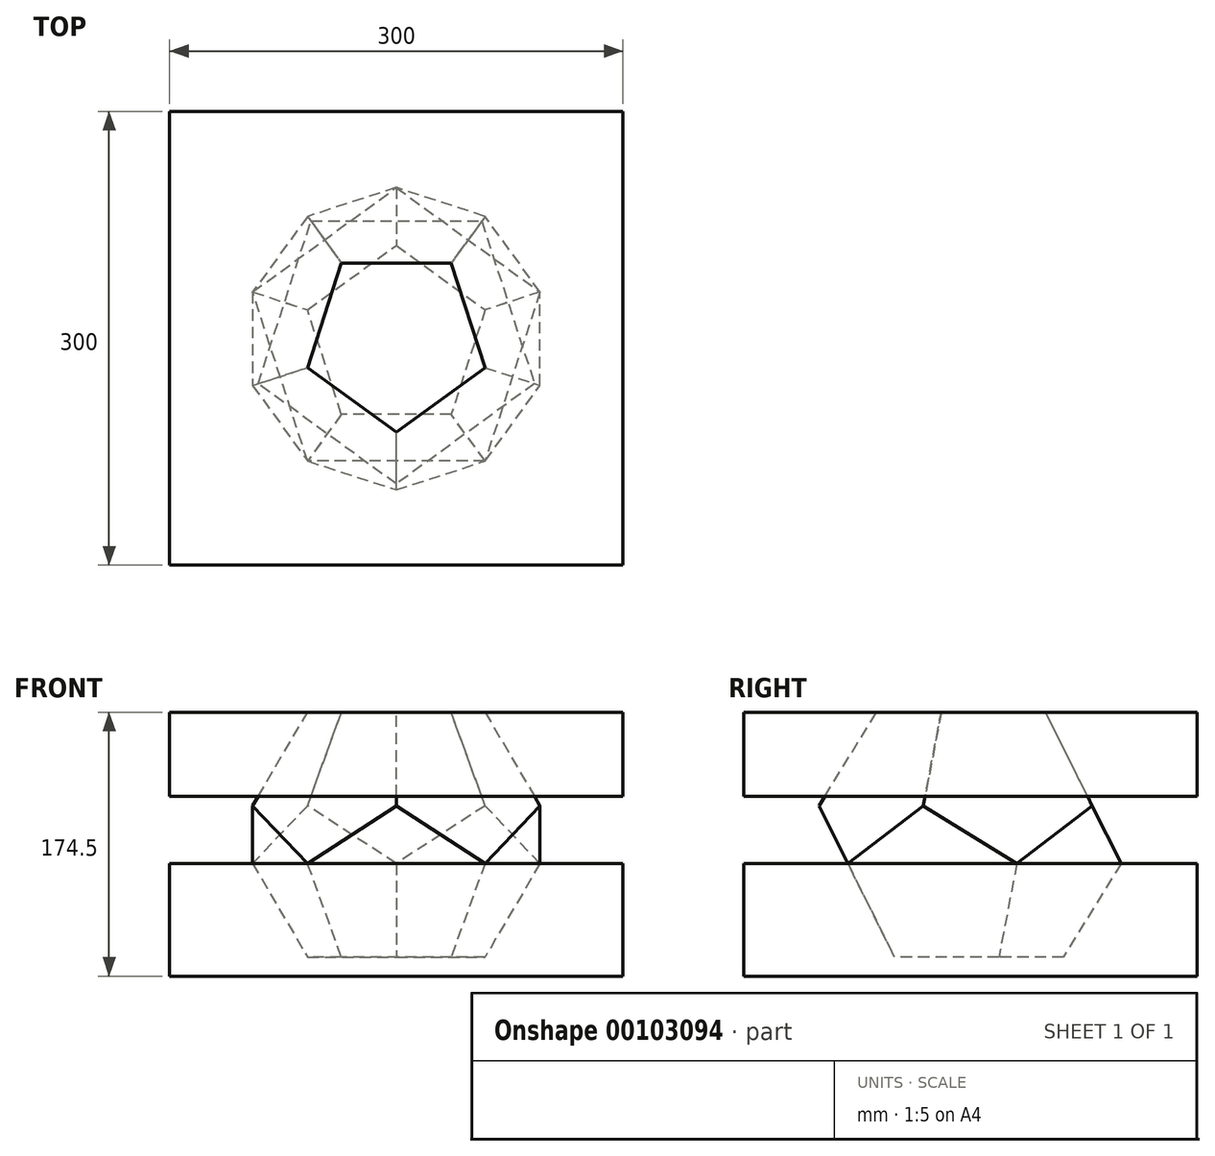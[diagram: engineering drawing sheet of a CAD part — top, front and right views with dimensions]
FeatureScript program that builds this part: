
annotation { "Feature Type Name" : "Feature", "Feature Type Description" : "" }
export const myFeature = defineFeature(function(context is Context, id is Id, definition is map)
    precondition{}
    {
        {
            var Q0;
            Q0=qCreatedBy(makeId("Top.planeOp"),FACE);
            var sketch = newSketch(context, id + "F0", { "sketchPlane" : qUnion([Q0])});
            skCircle(sketch, "E0.cCircle", {"center": v(0, 0) * mm, "radius": 50 * mm, "construction": true});
            skLineSegment(sketch, "E0.0", {"start": v(0, 61.8) * mm, "end": v(58.78, 19.1) * mm});
            skLineSegment(sketch, "E0.1", {"start": v(58.78, 19.1) * mm, "end": v(36.33, -50) * mm});
            skLineSegment(sketch, "E0.2", {"start": v(36.33, -50) * mm, "end": v(-36.33, -50) * mm});
            skLineSegment(sketch, "E0.3", {"start": v(-36.33, -50) * mm, "end": v(-58.78, 19.1) * mm});
            skLineSegment(sketch, "E0.4", {"start": v(-58.78, 19.1) * mm, "end": v(0, 61.8) * mm});
            skPoint(sketch, "E0.0.midPoint", {"position": v(29.39, 40.45) * mm});
            skSolve(sketch);
        }
        {
            var Q0;
            Q0=qCreatedBy(makeId("Right.planeOp"),FACE);
            var sketch = newSketch(context, id + "F1", { "sketchPlane" : qUnion([Q0])});
            skLineSegment(sketch, "E1", {"start": v(-50, 0) * mm, "end": v(-75.48, 50.96) * mm, "construction": true});
            skLineSegment(sketch, "E2", {"start": v(-50, 0) * mm, "end": v(0, 0) * mm, "construction": true});
            skLineSegment(sketch, "E3", {"start": v(0, 0) * mm, "end": v(0, 50.96) * mm, "construction": true});
            skSolve(sketch);
        }
        {
            var Q0;
            Q0=sQuery(id+"F0.wireOp",VERTEX,"E0.1.end");
            var Q1;
            Q1=sQuery(id+"F1.wireOp",VERTEX,"E1.start");
            var Q2;
            Q2=sQuery(id+"F1.wireOp",VERTEX,"E1.end");
            cPlane(context, id + "F2", {"entities" : qUnion([Q0, Q1, Q2]), "cplaneType" : CPlaneType.THREE_POINT, "offset" : 150 * mm, "width" : 150 * mm, "height" : 150 * mm});
        }
        {
            var Q0;
            Q0=qCreatedBy(id+"F2.planeOp",FACE);
            var sketch = newSketch(context, id + "F3", { "sketchPlane" : qUnion([Q0])});
            skCircle(sketch, "E4.cCircle", {"center": v(0, 72.36) * mm, "radius": 50 * mm, "construction": true});
            skLineSegment(sketch, "E4.0", {"start": v(36.33, 22.36) * mm, "end": v(-36.33, 22.36) * mm});
            skLineSegment(sketch, "E4.1", {"start": v(-36.33, 22.36) * mm, "end": v(-58.78, 91.46) * mm});
            skLineSegment(sketch, "E4.2", {"start": v(-58.78, 91.46) * mm, "end": v(0, 134.16) * mm});
            skLineSegment(sketch, "E4.3", {"start": v(0, 134.16) * mm, "end": v(58.78, 91.46) * mm});
            skLineSegment(sketch, "E4.4", {"start": v(58.78, 91.46) * mm, "end": v(36.33, 22.36) * mm});
            skPoint(sketch, "E4.0.midPoint", {"position": v(0, 22.36) * mm});
            skSolve(sketch);
        }
        {
            var Q0;
            Q0=qCreatedBy(makeId("Right.planeOp"),FACE);
            var sketch = newSketch(context, id + "F4", { "sketchPlane" : qUnion([Q0])});
            skLineSegment(sketch, "E5.0", {"start": v(-100, 100) * mm, "end": v(-80.9, 61.8) * mm, "construction": true});
            skLineSegment(sketch, "E6", {"start": v(-90.45, 80.9) * mm, "end": v(61.8, 80.9) * mm, "construction": true});
            skSolve(sketch);
        }
        {
            var Q0;
            Q0=makeQuery(id+"F0.imprint","IMPRINT",FACE,{"disambiguationData":[TD([[makeQuery(id+"F0.imprint","IMPRINT",EDGE,{"derivedFrom":sQuery(id+"F0.wireOp",EDGE,"E0.0")}),-1.0]])]});
            var Q1;
            Q1=qCreatedBy(id+"F2.planeOp",FACE);
            extrude(context, id + "F5", {"entities" : qUnion([Q0]), "endBoundEntity" : qUnion([Q1]), "depth" : 40 * mm});
        }
        {
            var Q0;
            Q0=makeQuery(id+"F3.imprint","IMPRINT",FACE,{"disambiguationData":[TD([[makeQuery(id+"F3.imprint","IMPRINT",EDGE,{"derivedFrom":sQuery(id+"F3.wireOp",EDGE,"E4.0")}),-1.0]])]});
            extrude(context, id + "F6", {"entities" : qUnion([Q0]), "oppositeDirection" : true, "depth" : 120 * mm});
        }
        {
            var Q0;
            Q0=makeQuery(id+"F6.opExtrude","SWEPT_BODY",BODY,{"disambiguationData":[OSD([sQuery(id+"F3.wireOp",EDGE,"E4.0"),sQuery(id+"F3.wireOp",EDGE,"E4.1"),sQuery(id+"F3.wireOp",EDGE,"E4.2"),sQuery(id+"F3.wireOp",EDGE,"E4.3"),sQuery(id+"F3.wireOp",EDGE,"E4.4")])]});
            var Q1;
            Q1=sQuery(id+"F1.wireOp",EDGE,"E3");
            circularPattern(context, id + "F7", {"entities" : qUnion([Q0]), "axis" : qUnion([Q1]), "angle" : 72 * degree, "instanceCount" : 5});
        }
        {
            var Q0;
            Q0=makeQuery(id+"F5.opExtrude","SWEPT_BODY",BODY,{"disambiguationData":[OSD([sQuery(id+"F0.wireOp",EDGE,"E0.0"),sQuery(id+"F0.wireOp",EDGE,"E0.1"),sQuery(id+"F0.wireOp",EDGE,"E0.2"),sQuery(id+"F0.wireOp",EDGE,"E0.3"),sQuery(id+"F0.wireOp",EDGE,"E0.4")])]});
            var Q1;
            Q1=makeQuery(id+"F6.opExtrude","SWEPT_BODY",BODY,{"disambiguationData":[OSD([sQuery(id+"F3.wireOp",EDGE,"E4.0"),sQuery(id+"F3.wireOp",EDGE,"E4.1"),sQuery(id+"F3.wireOp",EDGE,"E4.2"),sQuery(id+"F3.wireOp",EDGE,"E4.3"),sQuery(id+"F3.wireOp",EDGE,"E4.4")])]});
            var Q2;
            Q2=makeQuery(id+"F7.opPattern","COPY",BODY,{"derivedFrom":makeQuery(id+"F6.opExtrude","SWEPT_BODY",BODY,{"disambiguationData":[OSD([sQuery(id+"F3.wireOp",EDGE,"E4.0"),sQuery(id+"F3.wireOp",EDGE,"E4.1"),sQuery(id+"F3.wireOp",EDGE,"E4.2"),sQuery(id+"F3.wireOp",EDGE,"E4.3"),sQuery(id+"F3.wireOp",EDGE,"E4.4")])]}),"instanceName":"1"});
            var Q3;
            Q3=makeQuery(id+"F7.opPattern","COPY",BODY,{"derivedFrom":makeQuery(id+"F6.opExtrude","SWEPT_BODY",BODY,{"disambiguationData":[OSD([sQuery(id+"F3.wireOp",EDGE,"E4.0"),sQuery(id+"F3.wireOp",EDGE,"E4.1"),sQuery(id+"F3.wireOp",EDGE,"E4.2"),sQuery(id+"F3.wireOp",EDGE,"E4.3"),sQuery(id+"F3.wireOp",EDGE,"E4.4")])]}),"instanceName":"2"});
            var Q4;
            Q4=makeQuery(id+"F7.opPattern","COPY",BODY,{"derivedFrom":makeQuery(id+"F6.opExtrude","SWEPT_BODY",BODY,{"disambiguationData":[OSD([sQuery(id+"F3.wireOp",EDGE,"E4.0"),sQuery(id+"F3.wireOp",EDGE,"E4.1"),sQuery(id+"F3.wireOp",EDGE,"E4.2"),sQuery(id+"F3.wireOp",EDGE,"E4.3"),sQuery(id+"F3.wireOp",EDGE,"E4.4")])]}),"instanceName":"3"});
            var Q5;
            Q5=makeQuery(id+"F7.opPattern","COPY",BODY,{"derivedFrom":makeQuery(id+"F6.opExtrude","SWEPT_BODY",BODY,{"disambiguationData":[OSD([sQuery(id+"F3.wireOp",EDGE,"E4.0"),sQuery(id+"F3.wireOp",EDGE,"E4.1"),sQuery(id+"F3.wireOp",EDGE,"E4.2"),sQuery(id+"F3.wireOp",EDGE,"E4.3"),sQuery(id+"F3.wireOp",EDGE,"E4.4")])]}),"instanceName":"4"});
            var Q6;
            Q6=sQuery(id+"F4.wireOp",EDGE,"E6");
            transform(context, id + "F8", {"entities" : qUnion([Q0, Q1, Q2, Q3, Q4, Q5]), "transformType" : TransformType.ROTATION, "transformAxis" : qUnion([Q6]), "angle" : 180 * degree, "oppositeX" : false, "oppositeY" : false, "oppositeZ" : false, "makeCopy" : true});
        }
        {
            var Q0;
            Q0=makeQuery(id+"F8.opPattern","COPY",BODY,{"derivedFrom":makeQuery(id+"F7.opPattern","COPY",BODY,{"derivedFrom":makeQuery(id+"F6.opExtrude","SWEPT_BODY",BODY,{"disambiguationData":[OSD([sQuery(id+"F3.wireOp",EDGE,"E4.0"),sQuery(id+"F3.wireOp",EDGE,"E4.1"),sQuery(id+"F3.wireOp",EDGE,"E4.2"),sQuery(id+"F3.wireOp",EDGE,"E4.3"),sQuery(id+"F3.wireOp",EDGE,"E4.4")])]}),"instanceName":"2"}),"instanceName":"1"});
            var Q1;
            Q1=makeQuery(id+"F8.opPattern","COPY",BODY,{"derivedFrom":makeQuery(id+"F7.opPattern","COPY",BODY,{"derivedFrom":makeQuery(id+"F6.opExtrude","SWEPT_BODY",BODY,{"disambiguationData":[OSD([sQuery(id+"F3.wireOp",EDGE,"E4.0"),sQuery(id+"F3.wireOp",EDGE,"E4.1"),sQuery(id+"F3.wireOp",EDGE,"E4.2"),sQuery(id+"F3.wireOp",EDGE,"E4.3"),sQuery(id+"F3.wireOp",EDGE,"E4.4")])]}),"instanceName":"1"}),"instanceName":"1"});
            var Q2;
            Q2=makeQuery(id+"F8.opPattern","COPY",BODY,{"derivedFrom":makeQuery(id+"F6.opExtrude","SWEPT_BODY",BODY,{"disambiguationData":[OSD([sQuery(id+"F3.wireOp",EDGE,"E4.0"),sQuery(id+"F3.wireOp",EDGE,"E4.1"),sQuery(id+"F3.wireOp",EDGE,"E4.2"),sQuery(id+"F3.wireOp",EDGE,"E4.3"),sQuery(id+"F3.wireOp",EDGE,"E4.4")])]}),"instanceName":"1"});
            var Q3;
            Q3=makeQuery(id+"F8.opPattern","COPY",BODY,{"derivedFrom":makeQuery(id+"F7.opPattern","COPY",BODY,{"derivedFrom":makeQuery(id+"F6.opExtrude","SWEPT_BODY",BODY,{"disambiguationData":[OSD([sQuery(id+"F3.wireOp",EDGE,"E4.0"),sQuery(id+"F3.wireOp",EDGE,"E4.1"),sQuery(id+"F3.wireOp",EDGE,"E4.2"),sQuery(id+"F3.wireOp",EDGE,"E4.3"),sQuery(id+"F3.wireOp",EDGE,"E4.4")])]}),"instanceName":"4"}),"instanceName":"1"});
            var Q4;
            Q4=makeQuery(id+"F8.opPattern","COPY",BODY,{"derivedFrom":makeQuery(id+"F7.opPattern","COPY",BODY,{"derivedFrom":makeQuery(id+"F6.opExtrude","SWEPT_BODY",BODY,{"disambiguationData":[OSD([sQuery(id+"F3.wireOp",EDGE,"E4.0"),sQuery(id+"F3.wireOp",EDGE,"E4.1"),sQuery(id+"F3.wireOp",EDGE,"E4.2"),sQuery(id+"F3.wireOp",EDGE,"E4.3"),sQuery(id+"F3.wireOp",EDGE,"E4.4")])]}),"instanceName":"3"}),"instanceName":"1"});
            var Q5;
            Q5=makeQuery(id+"F8.opPattern","COPY",BODY,{"derivedFrom":makeQuery(id+"F5.opExtrude","SWEPT_BODY",BODY,{"disambiguationData":[OSD([sQuery(id+"F0.wireOp",EDGE,"E0.0"),sQuery(id+"F0.wireOp",EDGE,"E0.1"),sQuery(id+"F0.wireOp",EDGE,"E0.2"),sQuery(id+"F0.wireOp",EDGE,"E0.3"),sQuery(id+"F0.wireOp",EDGE,"E0.4")])]}),"instanceName":"1"});
            var Q6;
            Q6=sQuery(id+"F1.wireOp",EDGE,"E3");
            transform(context, id + "F9", {"entities" : qUnion([Q0, Q1, Q2, Q3, Q4, Q5]), "transformType" : TransformType.ROTATION, "transformAxis" : qUnion([Q6]), "angle" : 36 * degree, "oppositeX" : false, "oppositeY" : false, "oppositeZ" : false, "makeCopy" : false});
        }
        {
            var Q0;
            Q0=makeQuery(id+"F5.opExtrude","SWEPT_BODY",BODY,{"disambiguationData":[OSD([sQuery(id+"F0.wireOp",EDGE,"E0.0"),sQuery(id+"F0.wireOp",EDGE,"E0.1"),sQuery(id+"F0.wireOp",EDGE,"E0.2"),sQuery(id+"F0.wireOp",EDGE,"E0.3"),sQuery(id+"F0.wireOp",EDGE,"E0.4")])]});
            var Q1;
            Q1=makeQuery(id+"F6.opExtrude","SWEPT_BODY",BODY,{"disambiguationData":[OSD([sQuery(id+"F3.wireOp",EDGE,"E4.0"),sQuery(id+"F3.wireOp",EDGE,"E4.1"),sQuery(id+"F3.wireOp",EDGE,"E4.2"),sQuery(id+"F3.wireOp",EDGE,"E4.3"),sQuery(id+"F3.wireOp",EDGE,"E4.4")])]});
            var Q2;
            Q2=makeQuery(id+"F7.opPattern","COPY",BODY,{"derivedFrom":makeQuery(id+"F6.opExtrude","SWEPT_BODY",BODY,{"disambiguationData":[OSD([sQuery(id+"F3.wireOp",EDGE,"E4.0"),sQuery(id+"F3.wireOp",EDGE,"E4.1"),sQuery(id+"F3.wireOp",EDGE,"E4.2"),sQuery(id+"F3.wireOp",EDGE,"E4.3"),sQuery(id+"F3.wireOp",EDGE,"E4.4")])]}),"instanceName":"1"});
            var Q3;
            Q3=makeQuery(id+"F7.opPattern","COPY",BODY,{"derivedFrom":makeQuery(id+"F6.opExtrude","SWEPT_BODY",BODY,{"disambiguationData":[OSD([sQuery(id+"F3.wireOp",EDGE,"E4.0"),sQuery(id+"F3.wireOp",EDGE,"E4.1"),sQuery(id+"F3.wireOp",EDGE,"E4.2"),sQuery(id+"F3.wireOp",EDGE,"E4.3"),sQuery(id+"F3.wireOp",EDGE,"E4.4")])]}),"instanceName":"2"});
            var Q4;
            Q4=makeQuery(id+"F7.opPattern","COPY",BODY,{"derivedFrom":makeQuery(id+"F6.opExtrude","SWEPT_BODY",BODY,{"disambiguationData":[OSD([sQuery(id+"F3.wireOp",EDGE,"E4.0"),sQuery(id+"F3.wireOp",EDGE,"E4.1"),sQuery(id+"F3.wireOp",EDGE,"E4.2"),sQuery(id+"F3.wireOp",EDGE,"E4.3"),sQuery(id+"F3.wireOp",EDGE,"E4.4")])]}),"instanceName":"3"});
            var Q5;
            Q5=makeQuery(id+"F7.opPattern","COPY",BODY,{"derivedFrom":makeQuery(id+"F6.opExtrude","SWEPT_BODY",BODY,{"disambiguationData":[OSD([sQuery(id+"F3.wireOp",EDGE,"E4.0"),sQuery(id+"F3.wireOp",EDGE,"E4.1"),sQuery(id+"F3.wireOp",EDGE,"E4.2"),sQuery(id+"F3.wireOp",EDGE,"E4.3"),sQuery(id+"F3.wireOp",EDGE,"E4.4")])]}),"instanceName":"4"});
            var Q6;
            Q6=makeQuery(id+"F8.opPattern","COPY",BODY,{"derivedFrom":makeQuery(id+"F5.opExtrude","SWEPT_BODY",BODY,{"disambiguationData":[OSD([sQuery(id+"F0.wireOp",EDGE,"E0.0"),sQuery(id+"F0.wireOp",EDGE,"E0.1"),sQuery(id+"F0.wireOp",EDGE,"E0.2"),sQuery(id+"F0.wireOp",EDGE,"E0.3"),sQuery(id+"F0.wireOp",EDGE,"E0.4")])]}),"instanceName":"1"});
            var Q7;
            Q7=makeQuery(id+"F8.opPattern","COPY",BODY,{"derivedFrom":makeQuery(id+"F6.opExtrude","SWEPT_BODY",BODY,{"disambiguationData":[OSD([sQuery(id+"F3.wireOp",EDGE,"E4.0"),sQuery(id+"F3.wireOp",EDGE,"E4.1"),sQuery(id+"F3.wireOp",EDGE,"E4.2"),sQuery(id+"F3.wireOp",EDGE,"E4.3"),sQuery(id+"F3.wireOp",EDGE,"E4.4")])]}),"instanceName":"1"});
            var Q8;
            Q8=makeQuery(id+"F8.opPattern","COPY",BODY,{"derivedFrom":makeQuery(id+"F7.opPattern","COPY",BODY,{"derivedFrom":makeQuery(id+"F6.opExtrude","SWEPT_BODY",BODY,{"disambiguationData":[OSD([sQuery(id+"F3.wireOp",EDGE,"E4.0"),sQuery(id+"F3.wireOp",EDGE,"E4.1"),sQuery(id+"F3.wireOp",EDGE,"E4.2"),sQuery(id+"F3.wireOp",EDGE,"E4.3"),sQuery(id+"F3.wireOp",EDGE,"E4.4")])]}),"instanceName":"1"}),"instanceName":"1"});
            var Q9;
            Q9=makeQuery(id+"F8.opPattern","COPY",BODY,{"derivedFrom":makeQuery(id+"F7.opPattern","COPY",BODY,{"derivedFrom":makeQuery(id+"F6.opExtrude","SWEPT_BODY",BODY,{"disambiguationData":[OSD([sQuery(id+"F3.wireOp",EDGE,"E4.0"),sQuery(id+"F3.wireOp",EDGE,"E4.1"),sQuery(id+"F3.wireOp",EDGE,"E4.2"),sQuery(id+"F3.wireOp",EDGE,"E4.3"),sQuery(id+"F3.wireOp",EDGE,"E4.4")])]}),"instanceName":"2"}),"instanceName":"1"});
            var Q10;
            Q10=makeQuery(id+"F8.opPattern","COPY",BODY,{"derivedFrom":makeQuery(id+"F7.opPattern","COPY",BODY,{"derivedFrom":makeQuery(id+"F6.opExtrude","SWEPT_BODY",BODY,{"disambiguationData":[OSD([sQuery(id+"F3.wireOp",EDGE,"E4.0"),sQuery(id+"F3.wireOp",EDGE,"E4.1"),sQuery(id+"F3.wireOp",EDGE,"E4.2"),sQuery(id+"F3.wireOp",EDGE,"E4.3"),sQuery(id+"F3.wireOp",EDGE,"E4.4")])]}),"instanceName":"3"}),"instanceName":"1"});
            var Q11;
            Q11=makeQuery(id+"F8.opPattern","COPY",BODY,{"derivedFrom":makeQuery(id+"F7.opPattern","COPY",BODY,{"derivedFrom":makeQuery(id+"F6.opExtrude","SWEPT_BODY",BODY,{"disambiguationData":[OSD([sQuery(id+"F3.wireOp",EDGE,"E4.0"),sQuery(id+"F3.wireOp",EDGE,"E4.1"),sQuery(id+"F3.wireOp",EDGE,"E4.2"),sQuery(id+"F3.wireOp",EDGE,"E4.3"),sQuery(id+"F3.wireOp",EDGE,"E4.4")])]}),"instanceName":"4"}),"instanceName":"1"});
            booleanBodies(context, id + "F10", {"operationType" : BooleanOperationType.UNION, "tools" : qUnion([Q0, Q1, Q2, Q3, Q4, Q5, Q6, Q7, Q8, Q9, Q10, Q11])});
        }
        {
            var Q0;
            Q0=makeQuery(id+"F5.opExtrude","CAP_FACE",FACE,{"disambiguationData":[OSD([sQuery(id+"F0.wireOp",EDGE,"E0.0"),sQuery(id+"F0.wireOp",EDGE,"E0.1"),sQuery(id+"F0.wireOp",EDGE,"E0.2"),sQuery(id+"F0.wireOp",EDGE,"E0.3"),sQuery(id+"F0.wireOp",EDGE,"E0.4")])],"isStart":true});
            var sketch = newSketch(context, id + "F11", { "sketchPlane" : qUnion([Q0])});
            skLineSegment(sketch, "E7.bottom", {"start": v(150, 149.69) * mm, "end": v(-150, 149.69) * mm});
            skLineSegment(sketch, "E7.top", {"start": v(150, -150.31) * mm, "end": v(-150, -150.31) * mm});
            skLineSegment(sketch, "E7.left", {"start": v(150, 149.69) * mm, "end": v(150, -150.31) * mm});
            skLineSegment(sketch, "E7.right", {"start": v(-150, 149.69) * mm, "end": v(-150, -150.31) * mm});
            skPoint(sketch, "E7.middle", {"position": v(0, -0.31) * mm});
            skPoint(sketch, "E7.middle.positionSnap0", {"position": v(0, 50) * mm});
            skPoint(sketch, "E7.centerSnap0", {"position": v(0, 50) * mm});
            skSolve(sketch);
        }
        {
            var Q0;
            Q0=makeQuery(id+"F11.imprint","IMPRINT",FACE,{"disambiguationData":[TD([[makeQuery(id+"F11.imprint","IMPRINT",EDGE,{"derivedFrom":sQuery(id+"F11.wireOp",EDGE,"E7.bottom")}),1.0]])]});
            var Q1;
            {var subQ0=makeQuery(id+"F6.opExtrude","CAP_EDGE",EDGE,{"disambiguationData":[OSD([sQuery(id+"F3.wireOp",EDGE,"E4.0")])],"isStart":true});Q1=makeQuery(id+"F11.imprint","IMPRINT",FACE,{"disambiguationData":[TD([[makeQuery(id+"F11.imprint","IMPRINT",EDGE,{"derivedFrom":makeQuery(id+"F10.opBoolean","MERGE",EDGE,{"derivedFrom":[makeQuery(id+"F5.opExtrude","CAP_EDGE",EDGE,{"disambiguationData":[OSD([sQuery(id+"F0.wireOp",EDGE,"E0.0")])],"isStart":true}),makeQuery(id+"F7.opPattern","COPY",EDGE,{"derivedFrom":subQ0,"instanceName":"2"})]})}),1.0]])]});}
            var Q2;
            Q2=makeQuery(id+"F8.opPattern","COPY",FACE,{"derivedFrom":makeQuery(id+"F5.opExtrude","CAP_FACE",FACE,{"disambiguationData":[OSD([sQuery(id+"F0.wireOp",EDGE,"E0.0"),sQuery(id+"F0.wireOp",EDGE,"E0.1"),sQuery(id+"F0.wireOp",EDGE,"E0.2"),sQuery(id+"F0.wireOp",EDGE,"E0.3"),sQuery(id+"F0.wireOp",EDGE,"E0.4")])],"isStart":true}),"instanceName":"1"});
            extrude(context, id + "F12", {"entities" : qUnion([Q0, Q1]), "oppositeDirection" : true, "endBoundEntityFace" : qUnion([Q2]), "depth" : 61.74 * mm, "hasSecondDirection" : true, "secondDirectionOppositeDirection" : false, "secondDirectionDepth" : 12.7 * mm});
        }
        {
            var Q0;
            Q0=makeQuery(id+"F5.opExtrude","SWEPT_BODY",BODY,{"disambiguationData":[OSD([sQuery(id+"F0.wireOp",EDGE,"E0.0"),sQuery(id+"F0.wireOp",EDGE,"E0.1"),sQuery(id+"F0.wireOp",EDGE,"E0.2"),sQuery(id+"F0.wireOp",EDGE,"E0.3"),sQuery(id+"F0.wireOp",EDGE,"E0.4")])]});
            var Q1;
            Q1=makeQuery(id+"F12.opExtrude","SWEPT_BODY",BODY,{"disambiguationData":[OSD([sQuery(id+"F11.wireOp",EDGE,"E7.bottom"),sQuery(id+"F11.wireOp",EDGE,"E7.top"),sQuery(id+"F11.wireOp",EDGE,"E7.left"),sQuery(id+"F11.wireOp",EDGE,"E7.right")])]});
            booleanBodies(context, id + "F13", {"operationType" : BooleanOperationType.SUBTRACTION, "tools" : qUnion([Q0]), "targets" : qUnion([Q1]), "keepTools" : true});
        }
        {
            var Q0;
            Q0 = qSketchRegion(id + "F11", true);
            var Q1;
            Q1=makeQuery(id+"F8.opPattern","COPY",FACE,{"derivedFrom":makeQuery(id+"F5.opExtrude","CAP_FACE",FACE,{"disambiguationData":[OSD([sQuery(id+"F0.wireOp",EDGE,"E0.0"),sQuery(id+"F0.wireOp",EDGE,"E0.1"),sQuery(id+"F0.wireOp",EDGE,"E0.2"),sQuery(id+"F0.wireOp",EDGE,"E0.3"),sQuery(id+"F0.wireOp",EDGE,"E0.4")])],"isStart":true}),"instanceName":"1"});
            extrude(context, id + "F14", {"entities" : qUnion([Q0]), "endBound" : BoundingType.UP_TO_SURFACE, "oppositeDirection" : true, "endBoundEntityFace" : qUnion([Q1]), "depth" : 12.7 * mm, "hasSecondDirection" : true, "secondDirectionOppositeDirection" : true, "secondDirectionDepth" : 106.23 * mm});
        }
        {
            var Q0;
            Q0=makeQuery(id+"F5.opExtrude","SWEPT_BODY",BODY,{"disambiguationData":[OSD([sQuery(id+"F0.wireOp",EDGE,"E0.0"),sQuery(id+"F0.wireOp",EDGE,"E0.1"),sQuery(id+"F0.wireOp",EDGE,"E0.2"),sQuery(id+"F0.wireOp",EDGE,"E0.3"),sQuery(id+"F0.wireOp",EDGE,"E0.4")])]});
            var Q1;
            Q1=makeQuery(id+"F14.opExtrude","SWEPT_BODY",BODY,{"disambiguationData":[OSD([sQuery(id+"F11.wireOp",EDGE,"E7.bottom"),sQuery(id+"F11.wireOp",EDGE,"E7.top"),sQuery(id+"F11.wireOp",EDGE,"E7.left"),sQuery(id+"F11.wireOp",EDGE,"E7.right")])]});
            booleanBodies(context, id + "F15", {"operationType" : BooleanOperationType.SUBTRACTION, "tools" : qUnion([Q0]), "targets" : qUnion([Q1]), "keepTools" : true});
        }
    });
